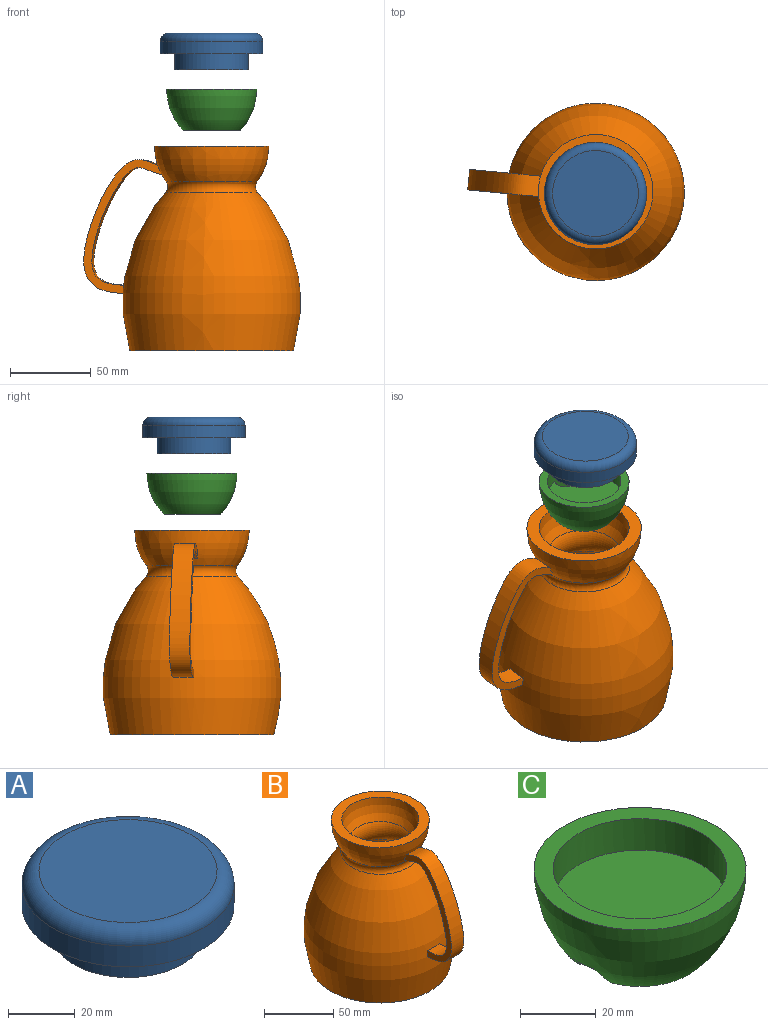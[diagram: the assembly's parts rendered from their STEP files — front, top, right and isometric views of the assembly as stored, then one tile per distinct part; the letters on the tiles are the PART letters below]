
ASSEMBLY  parts=3 mates=2
PART A: 6 faces, bbox 68.7x68.7x22.9 mm
  f0: cylinder r=22.86mm len=45.72mm, axis (0,0,1), area 1459.3mm2, adj f1,f4
  f1: plane 45.72x45.72mm, normal (0,0,-1), area 1641.7mm2, adj f0
  f2: cylinder r=31.75mm len=63.5mm, axis (0,0,-1), area 1520.1mm2, adj f4,f5
  f3: plane 53.34x53.34mm, normal (0,0,1), area 2234.6mm2, adj f5
  f4: plane 63.5x63.5mm, normal (0,0,-1), area 1525.2mm2, adj f0,f2
  f5: torus R=26.67mm, axis (0,0,1), area 1499.3mm2, adj f2,f3
PART B: 14 faces, bbox 110.5x134.6x127.1 mm
  f0: plane 101.6x101.6mm, normal (0,0,-1), area 8107.3mm2, adj f3
  f1: plane 71.12x71.12mm, normal (0,0,1), area 1520.1mm2, adj f2,f11
  f2: revolved ~71.12x71.12mm, area 4852.2mm2, adj f1,f4,f5,f6,f8,f9
  f3: revolved ~110.46x110.46mm, area 31984.5mm2, adj f0,f4,f6,f7,f8,f9
  f4: torus R=32.23mm, axis (0,0,1), area 1219.9mm2, adj f2,f3
  f5: plane 12.7x0.99mm, normal (0,0.96,-0.29), area 6.1mm2, adj f2,f6,f7,f8
  f6: plane 83.37x48.42mm, normal (1,0,0), area 598.8mm2, adj f2,f3,f5,f7,f9
  f7: bspline ~73.13x42.97mm, area 1404.6mm2, adj f3,f5,f6,f8
  f8: plane 83.37x48.42mm, normal (-1,0,0), area 598.8mm2, adj f2,f3,f5,f7,f9
  f9: bspline ~83.35x49.54mm, area 1570mm2, adj f2,f3,f6,f8
  f10: plane 89.97x89.97mm, normal (0,0,1), area 6357.8mm2, adj f12
  f11: revolved ~55.88x55.88mm, area 3071.2mm2, adj f1,f13
  f12: revolved ~95.22x95.22mm, area 23732.8mm2, adj f10,f13
  f13: torus R=32.23mm, axis (0,0,1), area 2273.3mm2, adj f11,f12
PART C: 6 faces, bbox 55.9x55.9x25.4 mm
  f0: plane 35.56x34.59mm, normal (0,0,-1), area 950.9mm2, adj f1,f5
  f1: revolved ~55.78x55.78mm, area 8513.3mm2, adj f0,f2,f3,f5
  f2: plane 55.88x55.88mm, normal (0,0,1), area 810.7mm2, adj f1,f3
  f3: cylinder r=22.86mm len=45.72mm, axis (0,0,1), area 1546.5mm2, adj f1,f2,f4,f5
  f4: plane 45.72x45.15mm, normal (0,0,1), area 1538.6mm2, adj f3,f5
  f5: cylinder r=6.14mm len=15.24mm, axis (0,0,1), area 367.6mm2, adj f0,f1,f3,f4
PLACE A t=(54.52,1.45,159.13)mm
PLACE B rot(axis=(0,0,-1),95.5deg) t=(54.64,2.66,-25.44)mm
PLACE C rot(axis=(0,0,-1),95.5deg) t=(54.64,2.66,111.45)mm
MATE cylindrical C.f3 <-> B.f4  axis (0,0,1) through (54.64,2.66,136.85)mm
MATE cylindrical A.f0 <-> C.f4  axis (0,0,-1) through (54.52,1.45,148.97)mm
